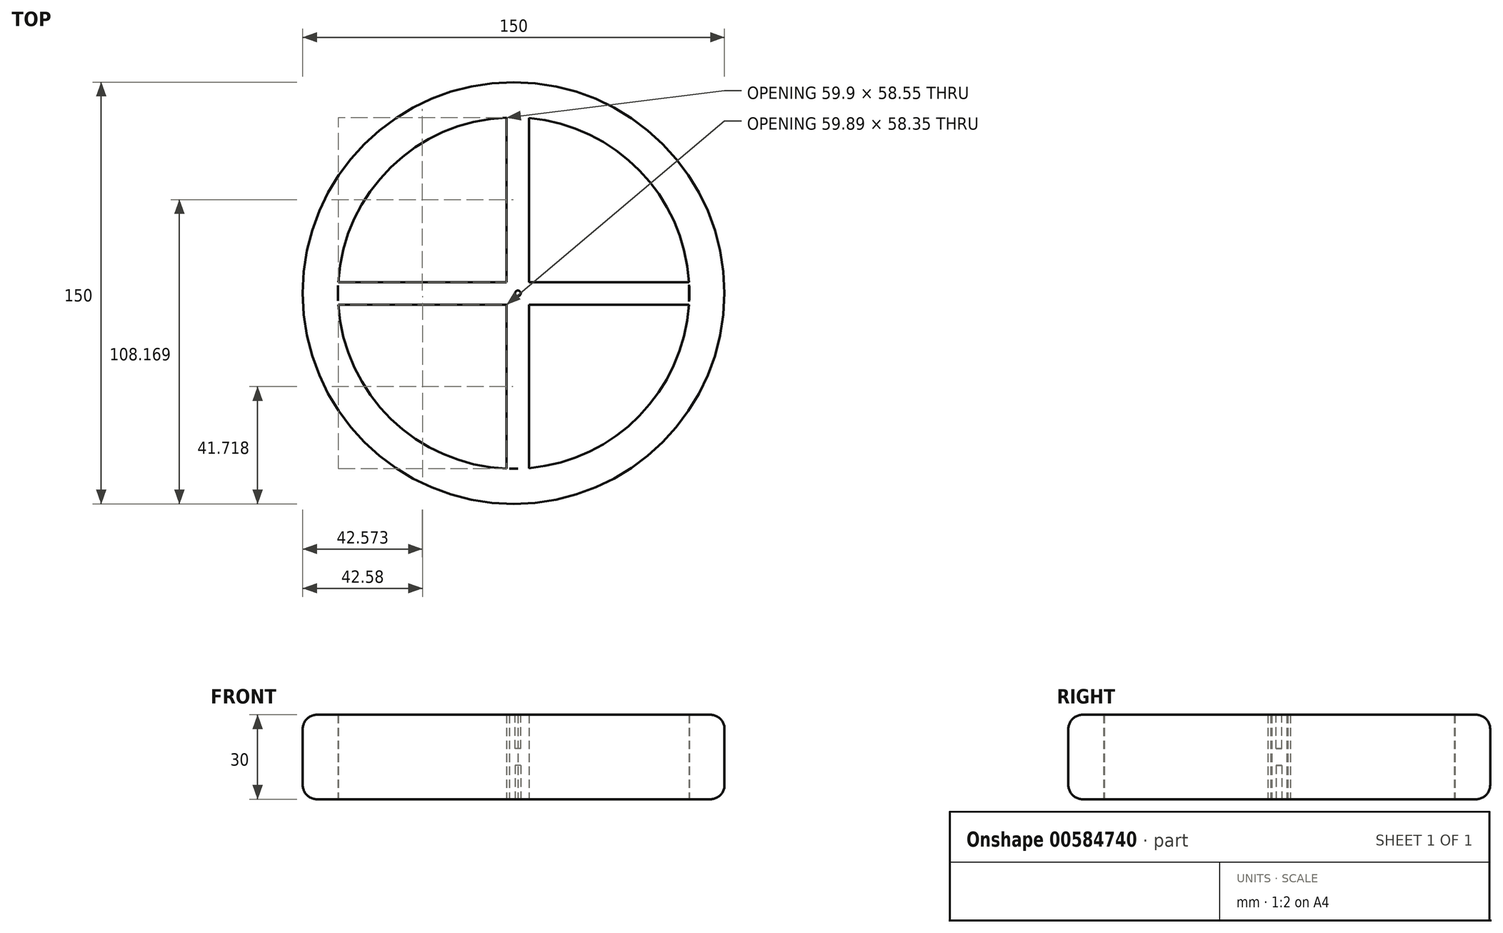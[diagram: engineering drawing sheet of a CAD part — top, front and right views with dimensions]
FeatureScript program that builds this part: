
annotation { "Feature Type Name" : "Feature", "Feature Type Description" : "" }
export const myFeature = defineFeature(function(context is Context, id is Id, definition is map)
    precondition{}
    {
        {
            var Q0;
            Q0=qCreatedBy(makeId("Top.planeOp"),FACE);
            var sketch = newSketch(context, id + "F0", { "sketchPlane" : qUnion([Q0])});
            skCircle(sketch, "E0", {"center": v(-35.88, 25.79) * mm, "radius": 75 * mm});
            skSolve(sketch);
        }
        {
            var Q0;
            Q0=makeQuery(id+"F0.imprint","IMPRINT",FACE,{"disambiguationData":[TD([[makeQuery(id+"F0.imprint","IMPRINT",EDGE,{"derivedFrom":sQuery(id+"F0.wireOp",EDGE,"E0")}),1.0]])]});
            extrude(context, id + "F1", {"entities" : qUnion([Q0]), "depth" : 30 * mm, "offsetDistance" : 25 * mm});
        }
        {
            var Q0;
            Q0=makeQuery(id+"F1.opExtrude","CAP_EDGE",EDGE,{"disambiguationData":[OSD([sQuery(id+"F0.wireOp",EDGE,"E0")])],"isStart":true});
            fillet(context, id + "F2", {"entities" : qUnion([Q0]), "radius" : 5 * mm, "tangentPropagation" : true, "allowEdgeOverflow" : false});
        }
        {
            var Q0;
            Q0=makeQuery(id+"F1.opExtrude","CAP_EDGE",EDGE,{"disambiguationData":[OSD([sQuery(id+"F0.wireOp",EDGE,"E0")])],"isStart":false});
            fillet(context, id + "F3", {"entities" : qUnion([Q0]), "radius" : 5 * mm, "tangentPropagation" : true, "allowEdgeOverflow" : false});
        }
        {
            var Q0;
            Q0=makeQuery(id+"F1.opExtrude","CAP_FACE",FACE,{"disambiguationData":[OSD([sQuery(id+"F0.wireOp",EDGE,"E0")])],"isStart":true});
            var sketch = newSketch(context, id + "F4", { "sketchPlane" : qUnion([Q0])});
            skCircle(sketch, "E1", {"center": v(-35.88, -25.79) * mm, "radius": 62.5 * mm});
            skSolve(sketch);
        }
        {
            var Q0;
            Q0=makeQuery(id+"F4.imprint","IMPRINT",FACE,{"disambiguationData":[TD([[makeQuery(id+"F4.imprint","IMPRINT",EDGE,{"derivedFrom":sQuery(id+"F4.wireOp",EDGE,"E1")}),1.0]])]});
            extrude(context, id + "F5", {"entities" : qUnion([Q0]), "operationType" : NewBodyOperationType.REMOVE, "oppositeDirection" : true, "depth" : 30 * mm, "offsetDistance" : 25 * mm});
        }
        {
            var Q0;
            Q0=makeQuery(id+"F1.opExtrude","CAP_FACE",FACE,{"disambiguationData":[OSD([sQuery(id+"F0.wireOp",EDGE,"E0")])],"isStart":true});
            var sketch = newSketch(context, id + "F6", { "sketchPlane" : qUnion([Q0])});
            skLineSegment(sketch, "E2", {"start": v(-34.36, -88.27) * mm, "end": v(-34.36, 36.7) * mm});
            skSolve(sketch);
        }
        {
            var Q0;
            Q0=sQuery(id+"F6.wireOp",EDGE,"E2");
            extrude(context, id + "F7", {"bodyType" : ToolBodyType.SURFACE, "operationType" : NewBodyOperationType.ADD, "surfaceEntities" : qUnion([Q0]), "oppositeDirection" : true, "depth" : 30 * mm, "offsetDistance" : 25 * mm});
        }
        {
            var Q0;
            Q0=makeQuery(id+"F7.opExtrude","SWEPT_FACE",FACE,{"disambiguationData":[OSD([sQuery(id+"F6.wireOp",EDGE,"E2")])]});
            extrude(context, id + "F8", {"entities" : qUnion([Q0]), "operationType" : NewBodyOperationType.ADD, "depth" : 8 * mm, "offsetDistance" : 25 * mm, "symmetric" : true});
        }
        {
            var Q0;
            Q0=qCreatedBy(makeId("Top.planeOp"),FACE);
            var sketch = newSketch(context, id + "F9", { "sketchPlane" : qUnion([Q0])});
            skLineSegment(sketch, "E3", {"start": v(-98.32, 25.68) * mm, "end": v(26.55, 25.68) * mm});
            skSolve(sketch);
        }
        {
            var Q0;
            Q0=qSketchRegion(id+"F9",true);
            var Q1;
            Q1=sQuery(id+"F9.wireOp",EDGE,"E3");
            extrude(context, id + "F10", {"entities" : qUnion([Q0]), "bodyType" : ToolBodyType.SURFACE, "operationType" : NewBodyOperationType.ADD, "surfaceEntities" : qUnion([Q1]), "depth" : 30 * mm, "offsetDistance" : 25 * mm});
        }
        {
            var Q0;
            Q0=makeQuery(id+"F10.opExtrude","SWEPT_FACE",FACE,{"disambiguationData":[OSD([sQuery(id+"F9.wireOp",EDGE,"E3")])]});
            extrude(context, id + "F11", {"entities" : qUnion([Q0]), "operationType" : NewBodyOperationType.ADD, "depth" : 8 * mm, "offsetDistance" : 25 * mm, "symmetric" : true});
        }
        {
            var Q0;
            {var subQ0=sQuery(id+"F9.wireOp",EDGE,"E3");var subQ1=sQuery(id+"F6.wireOp",EDGE,"E2");Q0=makeQuery(id+"F11.boolean.opBoolean","MERGE",FACE,{"derivedFrom":[makeQuery(id+"F8.boolean.opBoolean","MERGE",FACE,{"derivedFrom":[makeQuery(id+"F1.opExtrude","CAP_FACE",FACE,{"disambiguationData":[OSD([sQuery(id+"F0.wireOp",EDGE,"E0")])],"isStart":false}),makeQuery(id+"F8.opExtrude","SWEPT_FACE",FACE,{"disambiguationData":[OSD([subQ1]),TDD([makeQuery(id+"F7.opExtrude","CAP_EDGE",EDGE,{"disambiguationData":[OSD([subQ1])],"isStart":false})])]})]}),makeQuery(id+"F11.opExtrude","SWEPT_FACE",FACE,{"disambiguationData":[OSD([subQ0]),TDD([makeQuery(id+"F10.opExtrude","CAP_EDGE",EDGE,{"disambiguationData":[OSD([subQ0])],"isStart":false})])]})]});}
            var sketch = newSketch(context, id + "F12", { "sketchPlane" : qUnion([Q0])});
            skCircle(sketch, "E4", {"center": v(-34.35, 25.68) * mm, "radius": 1 * mm});
            skSolve(sketch);
        }
        {
            var Q0;
            Q0=makeQuery(id+"F12.imprint","IMPRINT",FACE,{"disambiguationData":[TD([[makeQuery(id+"F12.imprint","IMPRINT",EDGE,{"derivedFrom":sQuery(id+"F12.wireOp",EDGE,"E4")}),1.0]])]});
            extrude(context, id + "F13", {"entities" : qUnion([Q0]), "operationType" : NewBodyOperationType.REMOVE, "oppositeDirection" : true, "depth" : 12 * mm, "offsetDistance" : 25 * mm});
        }
        {
            var Q0;
            Q0=qCreatedBy(makeId("Top.planeOp"),FACE);
            var sketch = newSketch(context, id + "F14", { "sketchPlane" : qUnion([Q0])});
            skCircle(sketch, "E5", {"center": v(-34.36, 25.68) * mm, "radius": 1 * mm});
            skSolve(sketch);
        }
        {
            var Q0;
            Q0=makeQuery(id+"F14.imprint","IMPRINT",FACE,{"disambiguationData":[TD([[makeQuery(id+"F14.imprint","IMPRINT",EDGE,{"derivedFrom":sQuery(id+"F14.wireOp",EDGE,"E5")}),1.0]])]});
            extrude(context, id + "F15", {"entities" : qUnion([Q0]), "operationType" : NewBodyOperationType.REMOVE, "depth" : 12 * mm, "offsetDistance" : 25 * mm});
        }
    });
